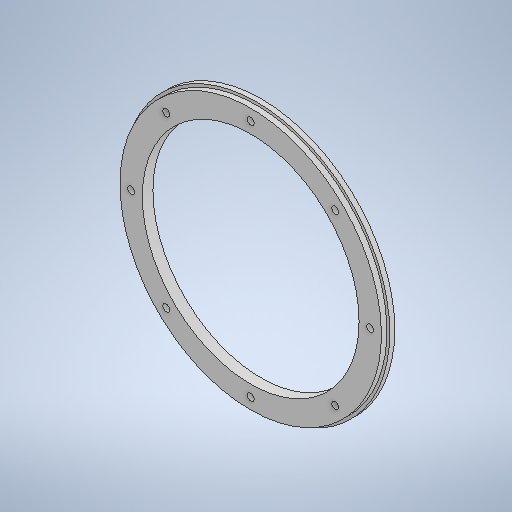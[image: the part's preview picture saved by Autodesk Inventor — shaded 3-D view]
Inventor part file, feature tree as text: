
AUTODESK INVENTOR PART (.ipt)
format: ipt  version: 2025 (Build 290162010, 162A)  size: 372,736 bytes
history: native  units: mm
features: extrude x5, sketch x5, other x2, pattern_circular x1, projected_geometry x1
ambient origin geometry x8: Origin, YZ Plane, XZ Plane, XY Plane, X Axis, Y Axis, Z Axis, Center Point
bodies: Solid1 (feature_tree)
feature tree (14):
  extrude  "Extrusion1"  Depth=389.0mm
  extrude  "Extrusion2"  Depth=12.5mm
  extrude  "Extrusion3"  Depth=80.0mm TaperAngle=360.0deg
  pattern_circular  "Circular Pattern1"  [2 undecoded]
  extrude  "Extrusion4"  Depth=9.0mm TaperAngle=0.0deg
  extrude  "Extrusion5"  Depth=19.0mm
  other  "A-Side Definition"
  sketch  "Sketch1"  dims[d0=40.0mm d1=389.0mm]
  sketch  "Sketch2"  dims[d2=38.0mm d3=0.0mm d4=12.5mm]
  projected_geometry  "Projected Loop1"
  sketch  "Sketch3"  dims[d5=0.0mm d6=0.0mm d7=80.0mm d8=360.0deg]
  sketch  "Sketch4"  dims[d10=27.5mm]
  sketch  "Sketch5"  dims[d11=11.0mm d12=0.0mm d13=5.0mm d14=9.0mm d15=0.0mm d16=38.0mm d17=19.0mm d18=0.0mm d19=0.0mm]
  other  "Definition1"
note: 2 required parameter values undecoded (feature->parameter linkage not recoverable at this tier; creation-order binding heuristic only, values carry confidence <= 0.55)
